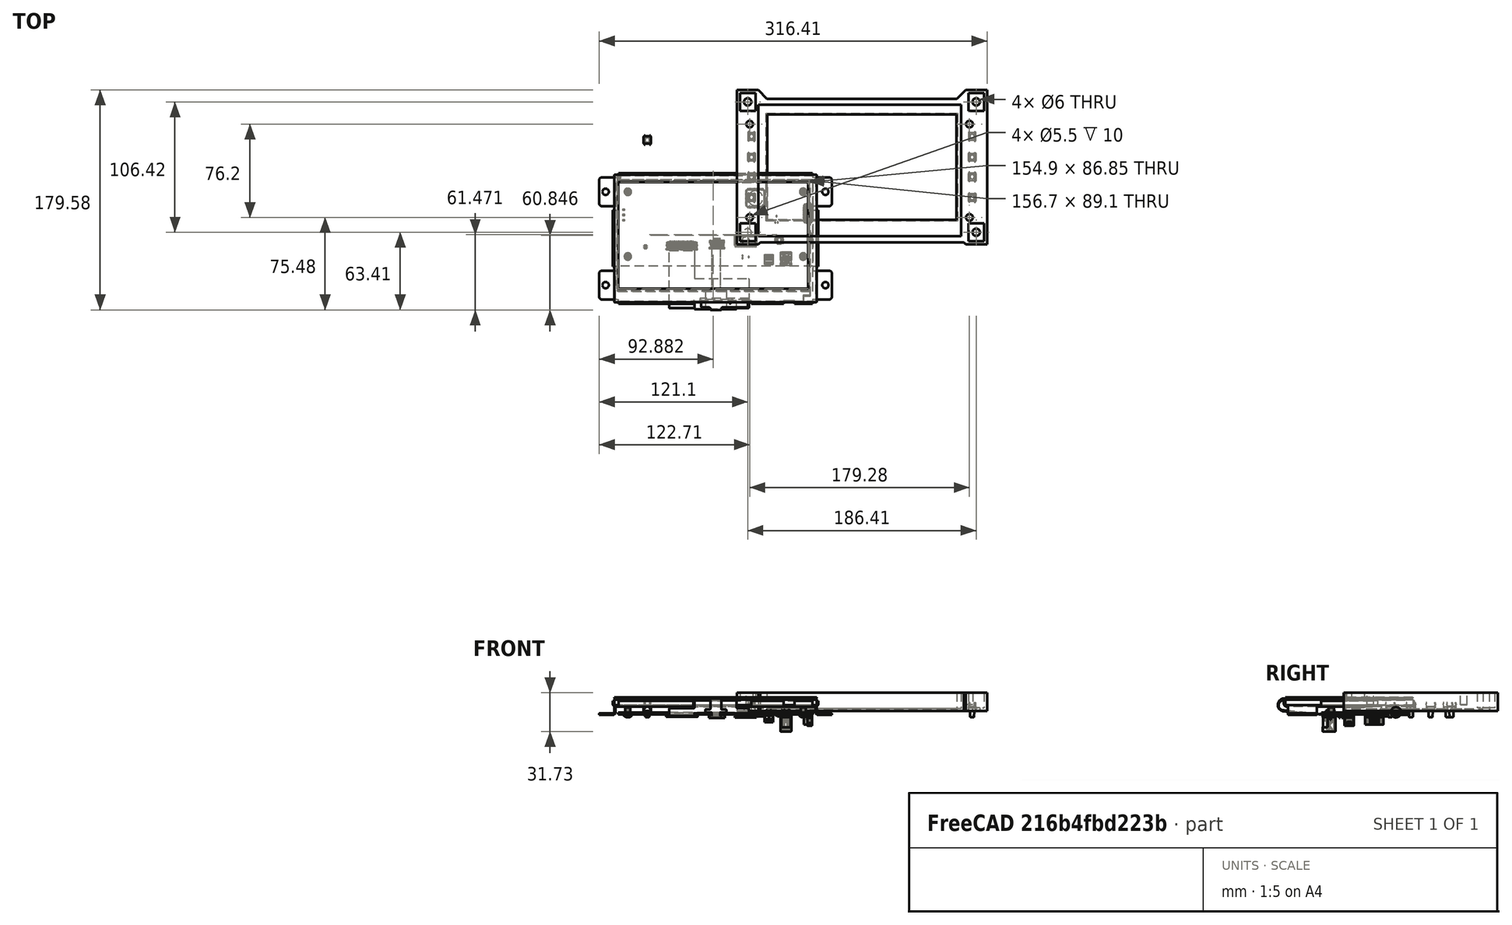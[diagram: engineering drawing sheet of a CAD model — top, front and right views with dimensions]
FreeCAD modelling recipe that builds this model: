
FCSTD DOCUMENT  (FreeCAD 0.18R4 (GitTag))
Label: front
License: All rights reserved
LicenseURL: http://en.wikipedia.org/wiki/All_rights_reserved
objects: Part::Feature×17, Sketcher::SketchObject×9, PartDesign::Pocket×6, PartDesign::Pad×1, PartDesign::Chamfer×1, PartDesign::Hole×1, App::Part×1, Mesh::Feature×1, PartDesign::Body×1
note: 44 computed .brp shape members not serialized (recipe doc carries the construction recipe); baked Part::Feature solids carry a one-line shape summary decoded from their .brp

FEATURE [Sketcher::SketchObject] Sketch  label="outerframe"
  MapMode = 5
  Support = -> [XY_Plane]
  sketch-geometry (4):
    g0: LineSegment StartX=0 StartY=0 StartZ=0 EndX=0 EndY=135.92 EndZ=0
    g1: LineSegment StartX=0 StartY=135.92 StartZ=0 EndX=204.21 EndY=135.92 EndZ=0
    g2: LineSegment StartX=204.21 StartY=135.92 StartZ=0 EndX=204.21 EndY=0 EndZ=0
    g3: LineSegment StartX=204.21 StartY=0 StartZ=0 EndX=0 EndY=0 EndZ=0
  constraints (11):
    c: Coincident(g0,g1)
    c: Coincident(g1,g2)
    c: Coincident(g2,g3)
    c: Coincident(g3,g0)
    c: Parallel(g3,g-1)
    c: Parallel(g0,g-2)
    c: Parallel(g2,g0)
    c: Parallel(g3,g1)
    c: DistanceY(g2,g1) = 135.92
    c: DistanceX(g0,g1) = 204.21
    c: Coincident(g0,g-1)
FEATURE [PartDesign::Pad] Pad  label="outer_frame"
  Length = 14.96
  Length2 = 100
  Profile = -> Sketch
  Type = 0
FEATURE [Sketcher::SketchObject] Sketch001  label="displayinlay"
  MapMode = 5
  Placement = pos=(0,0,14.96) rot=(0,0,1;0rad)
  Support = -> [Pad]
  sketch-geometry (4):
    g0: LineSegment StartX=17.65 StartY=118.77 StartZ=0 EndX=17.65 EndY=11.57 EndZ=0
    g1: LineSegment StartX=17.65 StartY=11.57 StartZ=0 EndX=182.95 EndY=11.57 EndZ=0
    g2: LineSegment StartX=182.95 StartY=11.57 StartZ=0 EndX=182.95 EndY=118.77 EndZ=0
    g3: LineSegment StartX=182.95 StartY=118.77 StartZ=0 EndX=17.65 EndY=118.77 EndZ=0
  constraints (12):
    c: Vertical(g0)
    c: Coincident(g0,g1)
    c: Horizontal(g1)
    c: Coincident(g1,g2)
    c: Coincident(g2,g3)
    c: Coincident(g3,g0)
    c: Horizontal(g3)
    c: Parallel(g0,g2)
    c: DistanceX(g0,g2) = 165.3
    c: DistanceY(g0,g0) = 107.2
    c: DistanceX(g-1,g0) = 17.65
    c: DistanceY(g-1,g0) = 11.57
FEATURE [PartDesign::Pocket] Pocket  label="display_inlay"
  BaseFeature = -> Pad
  Length = 12.96
  Length2 = 100
  Profile = -> Sketch001
  Type = 0
FEATURE [Sketcher::SketchObject] Sketch002  label="viewingarea"
  MapMode = 5
  Placement = pos=(0,0,14.96) rot=(0,0,1;0rad)
  Support = -> [Pocket]
  sketch-geometry (4):
    g0: LineSegment StartX=25 StartY=110.92 StartZ=0 EndX=25 EndY=25 EndZ=0
    g1: LineSegment StartX=25 StartY=25 StartZ=0 EndX=179.21 EndY=25 EndZ=0
    g2: LineSegment StartX=179.21 StartY=25 StartZ=0 EndX=179.21 EndY=110.92 EndZ=0
    g3: LineSegment StartX=179.21 StartY=110.92 StartZ=0 EndX=25 EndY=110.92 EndZ=0
  constraints (12):
    c: Vertical(g0)
    c: Coincident(g0,g1)
    c: Horizontal(g1)
    c: Coincident(g1,g2)
    c: Vertical(g2)
    c: Coincident(g2,g3)
    c: Coincident(g3,g0)
    c: Horizontal(g3)
    c: DistanceX(g0,g2) = 154.21
    c: DistanceY(g1,g2) = 85.92
    c: DistanceX(g-1,g0) = 25
    c: DistanceY(g-1,g0) = 25
FEATURE [PartDesign::Pocket] Pocket001  label="viewing_area"
  BaseFeature = -> Pocket
  Length = 14.96
  Length2 = 100
  Profile = -> Sketch002
  Type = 1
FEATURE [Sketcher::SketchObject] Sketch003  label="DisplayOutlines"
  MapMode = 5
  Placement = pos=(0,0,14.96) rot=(0,0,1;0rad)
  Support = -> [Pocket001]
  sketch-geometry (28):
    g0: LineSegment StartX=17.65 StartY=118.27 StartZ=0 EndX=17.65 EndY=11.57 EndZ=0
    g1: LineSegment StartX=17.65 StartY=11.57 StartZ=0 EndX=182.65 EndY=11.57 EndZ=0
    g2: LineSegment StartX=182.65 StartY=11.57 StartZ=0 EndX=182.65 EndY=118.27 EndZ=0
    g3: LineSegment StartX=182.65 StartY=118.27 StartZ=0 EndX=17.65 EndY=118.27 EndZ=0
    g4: LineSegment StartX=17.65 StartY=114.72 StartZ=0 EndX=17.65 EndY=91.32 EndZ=0
    g5: LineSegment StartX=17.65 StartY=91.32 StartZ=0 EndX=5.31 EndY=91.32 EndZ=0
    g6: LineSegment StartX=5.31 StartY=91.32 StartZ=0 EndX=5.31 EndY=114.72 EndZ=0
    g7: LineSegment StartX=5.31 StartY=114.72 StartZ=0 EndX=17.65 EndY=114.72 EndZ=0
    g8: Circle CenterX=10.51 CenterY=103.02 CenterZ=0 NormalX=0 NormalY=0 NormalZ=1 AngleXU=0 Radius=2.58
    g9: LineSegment StartX=5.31 StartY=38.52 StartZ=0 EndX=17.65 EndY=38.52 EndZ=0
    g10: LineSegment StartX=17.65 StartY=38.52 StartZ=0 EndX=17.65 EndY=15.12 EndZ=0
    g11: LineSegment StartX=17.65 StartY=15.12 StartZ=0 EndX=5.31 EndY=15.12 EndZ=0
    g12: LineSegment StartX=5.31 StartY=15.12 StartZ=0 EndX=5.31 EndY=38.52 EndZ=0
    g13: Circle CenterX=10.51 CenterY=26.82 CenterZ=0 NormalX=0 NormalY=0 NormalZ=1 AngleXU=0 Radius=2.58
    g14: LineSegment StartX=182.65 StartY=114.72 StartZ=0 EndX=194.99 EndY=114.72 EndZ=0
    g15: LineSegment StartX=194.99 StartY=114.72 StartZ=0 EndX=194.99 EndY=91.32 EndZ=0
    g16: LineSegment StartX=194.99 StartY=91.32 StartZ=0 EndX=182.65 EndY=91.32 EndZ=0
    g17: LineSegment StartX=182.65 StartY=91.32 StartZ=0 EndX=182.65 EndY=114.72 EndZ=0
    g18: Circle CenterX=189.79 CenterY=103.02 CenterZ=0 NormalX=0 NormalY=0 NormalZ=1 AngleXU=0 Radius=2.58
    g19: LineSegment StartX=182.65 StartY=38.52 StartZ=0 EndX=194.99 EndY=38.52 EndZ=0
    g20: LineSegment StartX=194.99 StartY=38.52 StartZ=0 EndX=194.99 EndY=15.12 EndZ=0
    g21: LineSegment StartX=194.99 StartY=15.12 StartZ=0 EndX=182.65 EndY=15.12 EndZ=0
    g22: LineSegment StartX=182.65 StartY=15.12 StartZ=0 EndX=182.65 EndY=38.52 EndZ=0
    g23: Circle CenterX=189.79 CenterY=26.82 CenterZ=0 NormalX=0 NormalY=0 NormalZ=1 AngleXU=0 Radius=2.58
    g24: LineSegment StartX=25 StartY=110.92 StartZ=0 EndX=25 EndY=25 EndZ=0
    g25: LineSegment StartX=25 StartY=25 StartZ=0 EndX=179.21 EndY=25 EndZ=0
    g26: LineSegment StartX=179.21 StartY=25 StartZ=0 EndX=179.21 EndY=110.92 EndZ=0
    g27: LineSegment StartX=179.21 StartY=110.92 StartZ=0 EndX=25 EndY=110.92 EndZ=0
  constraints (84):
    c: Vertical(g0)
    c: Coincident(g0,g1)
    c: Horizontal(g1)
    c: Coincident(g1,g2)
    c: Vertical(g2)
    c: Coincident(g2,g3)
    c: Parallel(g3,g1)
    c: Coincident(g3,g0)
    c: DistanceX(g0,g2) = 165
    c: DistanceY(g0,g0) = 106.7
    c: PointOnObject(g4,g0)
    c: Vertical(g4)
    c: Coincident(g4,g5)
    c: Horizontal(g5)
    c: Coincident(g5,g6)
    c: Coincident(g6,g7)
    c: Coincident(g7,g4)
    c: Parallel(g6,g0)
    c: Parallel(g7,g5)
    c: DistanceY(g5,g6) = 23.4
    c: DistanceX(g6,g4) = 12.34
    c: DistanceY(g4,g0) = 3.55
    c: Diameter(g8) = 5.16
    c: DistanceY(g8,g6) = 11.7
    c: DistanceX(g5,g8) = 5.2
    c: PointOnObject(g9,g0)
    c: Coincident(g9,g10)
    c: PointOnObject(g10,g0)
    c: Coincident(g10,g11)
    c: Coincident(g11,g12)
    c: Coincident(g12,g9)
    c: Parallel(g9,g11)
    c: Parallel(g12,g0)
    c: Perpendicular(g0,g9)
    c: DistanceY(g11,g9) = 23.4
    c: DistanceX(g9,g9) = 12.34
    c: DistanceY(g9,g5) = 52.8
    c: Diameter(g13) = 5.16
    c: DistanceY(g13,g9) = 11.7
    c: DistanceX(g9,g13) = 5.2
    c: PointOnObject(g14,g2)
    c: Horizontal(g14)
    c: Coincident(g14,g15)
    c: Vertical(g15)
    c: Coincident(g15,g16)
    c: Horizontal(g16)
    c: Coincident(g16,g17)
    c: Coincident(g17,g14)
    c: Vertical(g17)
    c: Diameter(g18) = 5.16
    c: DistanceX(g18,g14) = 5.2
    c: DistanceY(g18,g14) = 11.7
    c: DistanceY(g14,g2) = 3.55
    c: DistanceY(g15,g14) = 23.4
    c: DistanceX(g16,g15) = 12.34
    c: PointOnObject(g19,g2)
    c: Horizontal(g19)
    c: Coincident(g19,g20)
    c: Vertical(g20)
    c: Coincident(g20,g21)
    c: PointOnObject(g21,g2)
    c: Horizontal(g21)
    c: Coincident(g21,g22)
    c: Coincident(g22,g19)
    c: Diameter(g23) = 5.16
    c: DistanceX(g23,g19) = 5.2
    c: DistanceY(g19,g15) = 52.8
    c: DistanceY(g20,g19) = 23.4
    c: DistanceY(g20,g23) = 11.7
    c: DistanceX(g19,g19) = 12.34
    c: Vertical(g24)
    c: Coincident(g24,g25)
    c: Horizontal(g25)
    c: Coincident(g25,g26)
    c: Vertical(g26)
    c: Coincident(g26,g27)
    c: Coincident(g27,g24)
    c: Horizontal(g27)
    c: DistanceX(g24,g26) = 154.21
    c: DistanceY(g24,g24) = 85.92
    c: DistanceX(g10,g24) = 7.35
    c: DistanceY(g24,g0) = 7.35
    c: DistanceX(g-1,g24) = 25
    c: DistanceY(g-1,g24) = 25
FEATURE [Sketcher::SketchObject] Sketch005  label="EncoderCutOut"
  MapMode = 5
  Placement = pos=(0,0,14.96) rot=(0,0,1;0rad)
  sketch-geometry (16):
    g0: LineSegment StartX=2.5 StartY=128.42 StartZ=0 EndX=15.3 EndY=128.42 EndZ=0
    g1: LineSegment StartX=15.3 StartY=128.42 StartZ=0 EndX=15.3 EndY=113.92 EndZ=0
    g2: LineSegment StartX=15.3 StartY=113.92 StartZ=0 EndX=2.5 EndY=113.92 EndZ=0
    g3: LineSegment StartX=2.5 StartY=113.92 StartZ=0 EndX=2.5 EndY=128.42 EndZ=0
    g4: LineSegment StartX=188.91 StartY=128.42 StartZ=0 EndX=201.71 EndY=128.42 EndZ=0
    g5: LineSegment StartX=201.71 StartY=128.42 StartZ=0 EndX=201.71 EndY=113.92 EndZ=0
    g6: LineSegment StartX=201.71 StartY=113.92 StartZ=0 EndX=188.91 EndY=113.92 EndZ=0
    g7: LineSegment StartX=188.91 StartY=113.92 StartZ=0 EndX=188.91 EndY=128.42 EndZ=0
    g8: LineSegment StartX=2.5 StartY=22 StartZ=0 EndX=15.3 EndY=22 EndZ=0
    g9: LineSegment StartX=15.3 StartY=22 StartZ=0 EndX=15.3 EndY=7.5 EndZ=0
    g10: LineSegment StartX=15.3 StartY=7.5 StartZ=0 EndX=2.5 EndY=7.5 EndZ=0
    g11: LineSegment StartX=2.5 StartY=7.5 StartZ=0 EndX=2.5 EndY=22 EndZ=0
    g12: LineSegment StartX=188.91 StartY=22 StartZ=0 EndX=201.71 EndY=22 EndZ=0
    g13: LineSegment StartX=201.71 StartY=22 StartZ=0 EndX=201.71 EndY=7.5 EndZ=0
    g14: LineSegment StartX=201.71 StartY=7.5 StartZ=0 EndX=188.91 EndY=7.5 EndZ=0
    g15: LineSegment StartX=188.91 StartY=7.5 StartZ=0 EndX=188.91 EndY=22 EndZ=0
  constraints (48):
    c: Horizontal(g0)
    c: Coincident(g0,g1)
    c: Vertical(g1)
    c: Coincident(g1,g2)
    c: Horizontal(g2)
    c: Coincident(g2,g3)
    c: Coincident(g3,g0)
    c: Parallel(g3,g1)
    c: DistanceX(g0,g0) = 12.8
    c: DistanceY(g1,g0) = 14.5
    c: Horizontal(g4)
    c: Coincident(g4,g5)
    c: Vertical(g5)
    c: Coincident(g5,g6)
    c: Horizontal(g6)
    c: Coincident(g6,g7)
    c: Coincident(g7,g4)
    c: Parallel(g7,g5)
    c: Equal(g0,g4) = 12.8
    c: DistanceY(g5,g4) = 14.5
    c: Horizontal(g8)
    c: Coincident(g8,g9)
    c: Vertical(g9)
    c: Coincident(g9,g10)
    c: Horizontal(g10)
    c: Coincident(g10,g11)
    c: Coincident(g11,g8)
    c: Parallel(g11,g9)
    c: Equal(g0,g8) = 12.8
    c: DistanceY(g9,g8) = 14.5
    c: DistanceX(g-1,g10) = 2.5
    c: DistanceX(g-1,g2) = 2.5
    c: DistanceY(g-1,g10) = 7.5
    c: DistanceY(g-1,g0) = 128.42
    c: DistanceY(g-1,g4) = 128.42
    c: DistanceX(g-1,g4) = 201.71
    c: Horizontal(g12)
    c: Coincident(g12,g13)
    c: Vertical(g13)
    c: Coincident(g13,g14)
    c: Horizontal(g14)
    c: Coincident(g14,g15)
    c: Coincident(g15,g12)
    c: Parallel(g15,g13)
    c: DistanceY(g13,g12) = 14.5
    c: DistanceX(g12,g12) = 12.8
    c: DistanceY(g-1,g14) = 7.5
    c: DistanceX(g-1,g13) = 201.71
FEATURE [Sketcher::SketchObject] Sketch006  label="DisplayOutLinesHolesCut"
  MapMode = 5
  Placement = pos=(0,0,14.96) rot=(0,0,1;0rad)
  Support = -> [Pocket001]
  sketch-geometry (28):
    g0: LineSegment [constr] StartX=17.65 StartY=118.27 StartZ=0 EndX=17.65 EndY=11.57 EndZ=0
    g1: LineSegment [constr] StartX=17.65 StartY=11.57 StartZ=0 EndX=182.65 EndY=11.57 EndZ=0
    g2: LineSegment [constr] StartX=182.65 StartY=11.57 StartZ=0 EndX=182.65 EndY=118.27 EndZ=0
    g3: LineSegment [constr] StartX=182.65 StartY=118.27 StartZ=0 EndX=17.65 EndY=118.27 EndZ=0
    g4: LineSegment [constr] StartX=17.65 StartY=114.72 StartZ=0 EndX=17.65 EndY=91.32 EndZ=0
    g5: LineSegment [constr] StartX=17.65 StartY=91.32 StartZ=0 EndX=5.31 EndY=91.32 EndZ=0
    g6: LineSegment [constr] StartX=5.31 StartY=91.32 StartZ=0 EndX=5.31 EndY=114.72 EndZ=0
    g7: LineSegment [constr] StartX=5.31 StartY=114.72 StartZ=0 EndX=17.65 EndY=114.72 EndZ=0
    g8: Circle CenterX=10.51 CenterY=103.02 CenterZ=0 NormalX=0 NormalY=0 NormalZ=1 AngleXU=0 Radius=2.75
    g9: LineSegment [constr] StartX=5.31 StartY=38.52 StartZ=0 EndX=17.65 EndY=38.52 EndZ=0
    g10: LineSegment [constr] StartX=17.65 StartY=38.52 StartZ=0 EndX=17.65 EndY=15.12 EndZ=0
    g11: LineSegment [constr] StartX=17.65 StartY=15.12 StartZ=0 EndX=5.31 EndY=15.12 EndZ=0
    g12: LineSegment [constr] StartX=5.31 StartY=15.12 StartZ=0 EndX=5.31 EndY=38.52 EndZ=0
    g13: Circle CenterX=10.51 CenterY=26.82 CenterZ=0 NormalX=0 NormalY=0 NormalZ=1 AngleXU=0 Radius=2.75
    g14: LineSegment [constr] StartX=182.65 StartY=114.72 StartZ=0 EndX=194.99 EndY=114.72 EndZ=0
    g15: LineSegment [constr] StartX=194.99 StartY=114.72 StartZ=0 EndX=194.99 EndY=91.32 EndZ=0
    g16: LineSegment [constr] StartX=194.99 StartY=91.32 StartZ=0 EndX=182.65 EndY=91.32 EndZ=0
    g17: LineSegment [constr] StartX=182.65 StartY=91.32 StartZ=0 EndX=182.65 EndY=114.72 EndZ=0
    g18: Circle CenterX=189.79 CenterY=103.02 CenterZ=0 NormalX=0 NormalY=0 NormalZ=1 AngleXU=0 Radius=2.75
    g19: LineSegment [constr] StartX=182.65 StartY=38.52 StartZ=0 EndX=194.99 EndY=38.52 EndZ=0
    g20: LineSegment [constr] StartX=194.99 StartY=38.52 StartZ=0 EndX=194.99 EndY=15.12 EndZ=0
    g21: LineSegment [constr] StartX=194.99 StartY=15.12 StartZ=0 EndX=182.65 EndY=15.12 EndZ=0
    g22: LineSegment [constr] StartX=182.65 StartY=15.12 StartZ=0 EndX=182.65 EndY=38.52 EndZ=0
    g23: Circle CenterX=189.79 CenterY=26.82 CenterZ=0 NormalX=0 NormalY=0 NormalZ=1 AngleXU=0 Radius=2.75
    g24: LineSegment [constr] StartX=25 StartY=110.92 StartZ=0 EndX=25 EndY=25 EndZ=0
    g25: LineSegment [constr] StartX=25 StartY=25 StartZ=0 EndX=179.21 EndY=25 EndZ=0
    g26: LineSegment [constr] StartX=179.21 StartY=25 StartZ=0 EndX=179.21 EndY=110.92 EndZ=0
    g27: LineSegment [constr] StartX=179.21 StartY=110.92 StartZ=0 EndX=25 EndY=110.92 EndZ=0
  constraints (84):
    c: Vertical(g0)
    c: Coincident(g0,g1)
    c: Horizontal(g1)
    c: Coincident(g1,g2)
    c: Vertical(g2)
    c: Coincident(g2,g3)
    c: Parallel(g3,g1)
    c: Coincident(g3,g0)
    c: DistanceX(g0,g2) = 165
    c: DistanceY(g0,g0) = 106.7
    c: PointOnObject(g4,g0)
    c: Vertical(g4)
    c: Coincident(g4,g5)
    c: Horizontal(g5)
    c: Coincident(g5,g6)
    c: Coincident(g6,g7)
    c: Coincident(g7,g4)
    c: Parallel(g6,g0)
    c: Parallel(g7,g5)
    c: DistanceY(g5,g6) = 23.4
    c: DistanceX(g6,g4) = 12.34
    c: DistanceY(g4,g0) = 3.55
    c: Diameter(g8) = 5.5
    c: DistanceY(g8,g6) = 11.7
    c: DistanceX(g5,g8) = 5.2
    c: PointOnObject(g9,g0)
    c: Coincident(g9,g10)
    c: PointOnObject(g10,g0)
    c: Coincident(g10,g11)
    c: Coincident(g11,g12)
    c: Coincident(g12,g9)
    c: Parallel(g9,g11)
    c: Parallel(g12,g0)
    c: Perpendicular(g0,g9)
    c: DistanceY(g11,g9) = 23.4
    c: DistanceX(g9,g9) = 12.34
    c: DistanceY(g9,g5) = 52.8
    c: Diameter(g13) = 5.5
    c: DistanceY(g13,g9) = 11.7
    c: DistanceX(g9,g13) = 5.2
    c: PointOnObject(g14,g2)
    c: Horizontal(g14)
    c: Coincident(g14,g15)
    c: Vertical(g15)
    c: Coincident(g15,g16)
    c: Horizontal(g16)
    c: Coincident(g16,g17)
    c: Coincident(g17,g14)
    c: Vertical(g17)
    c: Diameter(g18) = 5.5
    c: DistanceX(g18,g14) = 5.2
    c: DistanceY(g18,g14) = 11.7
    c: DistanceY(g14,g2) = 3.55
    c: DistanceY(g15,g14) = 23.4
    c: DistanceX(g16,g15) = 12.34
    c: PointOnObject(g19,g2)
    c: Horizontal(g19)
    c: Coincident(g19,g20)
    c: Vertical(g20)
    c: Coincident(g20,g21)
    c: PointOnObject(g21,g2)
    c: Horizontal(g21)
    c: Coincident(g21,g22)
    c: Coincident(g22,g19)
    c: Diameter(g23) = 5.5
    c: DistanceX(g23,g19) = 5.2
    c: DistanceY(g19,g15) = 52.8
    c: DistanceY(g20,g19) = 23.4
    c: DistanceY(g20,g23) = 11.7
    c: DistanceX(g19,g19) = 12.34
    c: Vertical(g24)
    c: Coincident(g24,g25)
    c: Horizontal(g25)
    c: Coincident(g25,g26)
    c: Vertical(g26)
    c: Coincident(g26,g27)
    c: Coincident(g27,g24)
    c: Horizontal(g27)
    c: DistanceX(g24,g26) = 154.21
    c: DistanceY(g24,g24) = 85.92
    c: DistanceX(g10,g24) = 7.35
    c: DistanceY(g24,g0) = 7.35
    c: DistanceY(g-1,g24) = 25
    c: DistanceX(g-1,g24) = 25
FEATURE [PartDesign::Pocket] Pocket002  label="HolesDisplayMounting"
  BaseFeature = -> Pocket001
  Length = 10
  Length2 = 100
  Profile = -> Sketch006
  Type = 0
FEATURE [PartDesign::Chamfer] Chamfer
  Base = -> Pocket002 [Edge14,Edge13,Edge15,Edge12]
  BaseFeature = -> Pocket002
  Size = 1
FEATURE [Sketcher::SketchObject] Sketch007  label="EncoderCutOutHole"
  MapMode = 5
  Placement = pos=(0,0,14.96) rot=(0,0,1;0rad)
  sketch-geometry (32):
    g0: LineSegment [constr] StartX=2.5 StartY=128.42 StartZ=0 EndX=15.3 EndY=128.42 EndZ=0
    g1: LineSegment [constr] StartX=15.3 StartY=128.42 StartZ=0 EndX=15.3 EndY=113.92 EndZ=0
    g2: LineSegment [constr] StartX=15.3 StartY=113.92 StartZ=0 EndX=2.5 EndY=113.92 EndZ=0
    g3: LineSegment [constr] StartX=2.5 StartY=113.92 StartZ=0 EndX=2.5 EndY=128.42 EndZ=0
    g4: Circle CenterX=8.9 CenterY=121.17 CenterZ=0 NormalX=0 NormalY=0 NormalZ=1 AngleXU=0 Radius=3.5
    g5: LineSegment [constr] StartX=2.5 StartY=113.92 StartZ=0 EndX=15.3 EndY=128.42 EndZ=0
    g6: LineSegment [constr] StartX=15.3 StartY=113.92 StartZ=0 EndX=2.5 EndY=128.42 EndZ=0
    g7: GeomPoint X=8.9 Y=121.17 Z=0
    g8: LineSegment [constr] StartX=2.5 StartY=22 StartZ=0 EndX=15.3 EndY=22 EndZ=0
    g9: LineSegment [constr] StartX=15.3 StartY=22 StartZ=0 EndX=15.3 EndY=7.5 EndZ=0
    g10: LineSegment [constr] StartX=15.3 StartY=7.5 StartZ=0 EndX=2.5 EndY=7.5 EndZ=0
    g11: LineSegment [constr] StartX=2.5 StartY=7.5 StartZ=0 EndX=2.5 EndY=22 EndZ=0
    g12: Circle CenterX=8.9 CenterY=14.75 CenterZ=0 NormalX=0 NormalY=0 NormalZ=1 AngleXU=0 Radius=3.5
    g13: LineSegment [constr] StartX=2.5 StartY=7.5 StartZ=0 EndX=15.3 EndY=22 EndZ=0
    g14: LineSegment [constr] StartX=15.3 StartY=7.5 StartZ=0 EndX=2.5 EndY=22 EndZ=0
    g15: GeomPoint X=8.9 Y=14.75 Z=0
    g16: LineSegment [constr] StartX=188.91 StartY=128.42 StartZ=0 EndX=201.71 EndY=128.42 EndZ=0
    g17: LineSegment [constr] StartX=201.71 StartY=128.42 StartZ=0 EndX=201.71 EndY=113.92 EndZ=0
    g18: LineSegment [constr] StartX=201.71 StartY=113.92 StartZ=0 EndX=188.91 EndY=113.92 EndZ=0
    g19: LineSegment [constr] StartX=188.91 StartY=113.92 StartZ=0 EndX=188.91 EndY=128.42 EndZ=0
    g20: Circle CenterX=195.31 CenterY=121.17 CenterZ=0 NormalX=0 NormalY=0 NormalZ=1 AngleXU=0 Radius=3.5
    g21: LineSegment [constr] StartX=188.91 StartY=113.92 StartZ=0 EndX=201.71 EndY=128.42 EndZ=0
    g22: LineSegment [constr] StartX=201.71 StartY=113.92 StartZ=0 EndX=188.91 EndY=128.42 EndZ=0
    g23: GeomPoint X=195.31 Y=121.17 Z=0
    g24: LineSegment [constr] StartX=188.91 StartY=22 StartZ=0 EndX=201.71 EndY=22 EndZ=0
    g25: LineSegment [constr] StartX=201.71 StartY=22 StartZ=0 EndX=201.71 EndY=7.5 EndZ=0
    g26: LineSegment [constr] StartX=201.71 StartY=7.5 StartZ=0 EndX=188.91 EndY=7.5 EndZ=0
    g27: LineSegment [constr] StartX=188.91 StartY=7.5 StartZ=0 EndX=188.91 EndY=22 EndZ=0
    g28: Circle CenterX=195.31 CenterY=14.75 CenterZ=0 NormalX=0 NormalY=0 NormalZ=1 AngleXU=0 Radius=3.5
    g29: LineSegment [constr] StartX=188.91 StartY=7.5 StartZ=0 EndX=201.71 EndY=22 EndZ=0
    g30: LineSegment [constr] StartX=201.71 StartY=7.5 StartZ=0 EndX=188.91 EndY=22 EndZ=0
    g31: GeomPoint X=195.31 Y=14.75 Z=0
  constraints (84):
    c: Horizontal(g0)
    c: Coincident(g0,g1)
    c: Vertical(g1)
    c: Coincident(g1,g2)
    c: Horizontal(g2)
    c: Coincident(g2,g3)
    c: Coincident(g3,g0)
    c: Parallel(g3,g1)
    c: DistanceX(g0,g0) = 12.8
    c: DistanceY(g1,g0) = 14.5
    c: Diameter(g4) = 7
    c: Coincident(g5,g2)
    c: Coincident(g5,g0)
    c: Coincident(g6,g1)
    c: Coincident(g6,g0)
    c: PointOnObject(g7,g5)
    c: PointOnObject(g7,g6)
    c: DistanceY(g4,g7) = 0
    c: DistanceX(g7,g4) = 0
    c: Horizontal(g8)
    c: Coincident(g8,g9)
    c: Vertical(g9)
    c: Coincident(g9,g10)
    c: Horizontal(g10)
    c: Coincident(g10,g11)
    c: Coincident(g11,g8)
    c: Parallel(g11,g9)
    c: Equal(g0,g8) = 12.8
    c: DistanceY(g9,g8) = 14.5
    c: Equal(g4,g12) = 7
    c: Coincident(g13,g10)
    c: Coincident(g13,g8)
    c: Coincident(g14,g9)
    c: Coincident(g14,g8)
    c: PointOnObject(g15,g13)
    c: PointOnObject(g15,g14)
    c: DistanceY(g12,g15) = 0
    c: DistanceX(g15,g12) = 0
    c: Horizontal(g16)
    c: Coincident(g16,g17)
    c: Vertical(g17)
    c: Coincident(g17,g18)
    c: Horizontal(g18)
    c: Coincident(g18,g19)
    c: Coincident(g19,g16)
    c: Parallel(g19,g17)
    c: Equal(g0,g16) = 12.8
    c: DistanceY(g17,g16) = 14.5
    c: Equal(g4,g20) = 7
    c: Coincident(g21,g18)
    c: Coincident(g21,g16)
    c: Coincident(g22,g17)
    c: Coincident(g22,g16)
    c: PointOnObject(g23,g21)
    c: PointOnObject(g23,g22)
    c: DistanceY(g20,g23) = 0
    c: DistanceX(g23,g20) = 0
    c: Horizontal(g24)
    c: Coincident(g24,g25)
    c: Vertical(g25)
    c: Coincident(g25,g26)
    c: Horizontal(g26)
    c: Coincident(g26,g27)
    c: Coincident(g27,g24)
    c: Parallel(g27,g25)
    c: Equal(g0,g24) = 12.8
    c: DistanceY(g25,g24) = 14.5
    c: Equal(g4,g28) = 7
    c: Coincident(g29,g26)
    c: Coincident(g29,g24)
    c: Coincident(g30,g25)
    c: Coincident(g30,g24)
    c: PointOnObject(g31,g29)
    c: PointOnObject(g31,g30)
    c: DistanceY(g28,g31) = 0
    c: DistanceX(g31,g28) = 0
    c: DistanceX(g-1,g2) = 2.5
    c: DistanceX(g-1,g10) = 2.5
    c: DistanceX(g-1,g25) = 201.71
    c: DistanceX(g-1,g17) = 201.71
    c: DistanceY(g-1,g10) = 7.5
    c: DistanceY(g-1,g25) = 7.5
    c: DistanceY(g-1,g0) = 128.42
    c: DistanceY(g-1,g16) = 128.42
FEATURE [PartDesign::Pocket] Pocket003  label="EncoderPocket"
  BaseFeature = -> Chamfer
  Length = 12.46
  Length2 = 100
  Profile = -> Sketch005
  Type = 0
FEATURE [PartDesign::Hole] Hole  label="EncoderHoles"
  BaseFeature = -> Pocket003
  Depth = 25
  DepthType = 0
  Diameter = 6
  DrillPoint = 1
  DrillPointAngle = 118
  HoleCutCountersinkAngle = 90
  HoleCutDepth = 0
  HoleCutDiameter = 0
  HoleCutType = 0
  ModelActualThread = false
  Profile = -> Sketch007
  Tapered = false
  TaperedAngle = 90
  ThreadAngle = 0
  ThreadClass = 0
  ThreadCutOffInner = 0
  ThreadCutOffOuter = 0
  ThreadDirection = 0
  ThreadFit = 0
  ThreadPitch = 0
  ThreadSize = 0
  ThreadType = 0
  Threaded = false
FEATURE [Sketcher::SketchObject] Sketch008  label="Trim"
  MapMode = 5
  Placement = pos=(0,0,14.96) rot=(0,0,1;0rad)
  Support = -> [Hole]
  sketch-geometry (17):
    g0: LineSegment StartX=0 StartY=130.92 StartZ=0 EndX=0 EndY=135.92 EndZ=0
    g1: LineSegment StartX=0 StartY=135.92 StartZ=0 EndX=10 EndY=135.92 EndZ=0
    g2: LineSegment StartX=0 StartY=130.92 StartZ=0 EndX=17.5 EndY=130.92 EndZ=0
    g3: LineSegment StartX=17.5 StartY=130.92 StartZ=0 EndX=24.65 EndY=123.77 EndZ=0
    g4: LineSegment StartX=24.65 StartY=123.77 StartZ=0 EndX=179.56 EndY=123.77 EndZ=0
    g5: LineSegment StartX=179.56 StartY=123.77 StartZ=0 EndX=186.71 EndY=130.92 EndZ=0
    g6: LineSegment StartX=186.71 StartY=130.92 StartZ=0 EndX=204.21 EndY=130.92 EndZ=0
    g7: LineSegment StartX=204.21 StartY=130.92 StartZ=0 EndX=204.21 EndY=135.92 EndZ=0
    g8: LineSegment StartX=204.21 StartY=135.92 StartZ=0 EndX=0 EndY=135.92 EndZ=0
    g9: LineSegment StartX=0 StartY=0 StartZ=0 EndX=204.21 EndY=0 EndZ=0
    g10: LineSegment StartX=204.21 StartY=0 StartZ=0 EndX=204.21 EndY=5 EndZ=0
    g11: LineSegment StartX=204.21 StartY=5 StartZ=0 EndX=186.71 EndY=5 EndZ=0
    g12: LineSegment StartX=186.71 StartY=5 StartZ=0 EndX=185.14 EndY=6.57 EndZ=0
    g13: LineSegment StartX=185.14 StartY=6.57 StartZ=0 EndX=19.07 EndY=6.57 EndZ=0
    g14: LineSegment StartX=19.07 StartY=6.57 StartZ=0 EndX=17.5 EndY=5 EndZ=0
    g15: LineSegment StartX=17.5 StartY=5 StartZ=0 EndX=0 EndY=5 EndZ=0
    g16: LineSegment StartX=0 StartY=5 StartZ=0 EndX=0 EndY=0 EndZ=0
  constraints (50):
    c: DistanceX(g-1,g1) = 10
    c: DistanceY(g-1,g1) = 135.92
    c: Coincident(g0,g1)
    c: Horizontal(g1)
    c: Horizontal(g2)
    c: Coincident(g2,g3)
    c: Coincident(g3,g4)
    c: Horizontal(g4)
    c: Coincident(g4,g5)
    c: Coincident(g5,g6)
    c: Horizontal(g6)
    c: Coincident(g6,g7)
    c: Vertical(g7)
    c: Coincident(g7,g8)
    c: Coincident(g8,g0)
    c: Horizontal(g8)
    c: Coincident(g2,g0)
    c: Parallel(g7,g0)
    c: DistanceX(g-1,g0) = 0
    c: DistanceX(g-1,g7) = 204.21
    c: Angle(g5) = 0.785398
    c: Angle(g3) = -0.785398
    c: DistanceY(g6,g0) = 0
    c: DistanceX(g-1,g2) = 17.5
    c: DistanceX(g-1,g5) = 186.71
    c: DistanceY(g-1,g2) = 130.92
    c: DistanceY(g-1,g3) = 123.77
    c: Coincident(g-1,g9)
    c: PointOnObject(g9,g-1)
    c: Coincident(g9,g10)
    c: Coincident(g10,g11)
    c: Coincident(g11,g12)
    c: Coincident(g12,g13)
    c: Horizontal(g13)
    c: Coincident(g13,g14)
    c: Coincident(g14,g15)
    c: Coincident(g15,g16)
    c: Coincident(g16,g9)
    c: Vertical(g16)
    c: Parallel(g15,g9)
    c: Parallel(g11,g9)
    c: Angle(g12) = 2.35619
    c: Angle(g14) = -2.35619
    c: Perpendicular(g9,g10)
    c: DistanceX(g9,g9) = 204.21
    c: DistanceY(g9,g15) = 5
    c: DistanceY(g11,g14) = 0
    c: DistanceY(g9,g13) = 6.57
    c: DistanceX(g9,g14) = 17.5
    c: DistanceX(g9,g11) = 186.71
FEATURE [Part::Feature] Part__Feature007  label="SCREW_95836A206"
  Placement = pos=(-88.858,-5.03851,2.22572) rot=(-0.001042,0.999999,0;3.14159rad)
  shape: bbox 6.495 x 6.495 x 7.739 mm, 90 faces (baked)
FEATURE [Part::Feature] Part__Feature004  label="SCREW_95836A203"
  Placement = pos=(54.142,47.7615,2.22572) rot=(0.112264,0.993678,0;3.14159rad)
  shape: bbox 6.516 x 6.331 x 7.739 mm, 90 faces (baked)
FEATURE [Part::Feature] Part__Feature006  label="SCREW_95836A205"
  Placement = pos=(-88.858,47.7615,2.22572) rot=(-0.100524,0.994935,0;3.14159rad)
  shape: bbox 6.449 x 6.363 x 7.739 mm, 90 faces (baked)
FEATURE [Part::Feature] Part__Feature005  label="SCREW_95836A204"
  Placement = pos=(54.142,-5.03851,2.22572) rot=(-0.016203,0.999869,0;3.14159rad)
  shape: bbox 6.491 x 6.491 x 7.739 mm, 90 faces (baked)
FEATURE [Part::Feature] Part__Feature  label="NHD-7.0-Mount"
  Placement = pos=(-66.5026,-96.831,-149.328) rot=(0,0,1;0rad)
  shape: bbox 189.7 x 106.7 x 11.46 mm, 298 faces, 5 solids (baked)
FEATURE [Part::Feature] Part__Feature001  label="NHD-7.0-1024600AF-LSXP"
  Placement = pos=(-17.358,9.66149,4.82572) rot=(0,0,1;0rad)
  shape: bbox 165 x 109.7 x 14.12 mm, 201 faces (baked)
FEATURE [Part::Feature] Part__Feature003  label="NHD-7.0-HDMI_PCB"
  Placement = pos=(-100.679,-3.63887,23.5082) rot=(0,1,0;3.14159rad)
  shape: bbox 159 x 68.8 x 17.6 mm, 5848 faces, 33 solids (baked)
FEATURE [Part::Feature] Part__Feature002  label="NHD-CTP-7.0K-HR"
  Placement = pos=(-14.4254,7.67152,10.6757) rot=(0,0,1;0rad)
  shape: bbox 165 x 110.3 x 15.54 mm, 144 faces, 8 solids (baked)
FEATURE [App::Part] NHD_7_0_HDMI_HR_RSXP_CTU  label="NHD-7.0-HDMI-HR-RSXP-CTU"
  Group = -> [Part__Feature,Part__Feature001,Part__Feature002,Part__Feature003,Part__Feature004,Part__Feature005,Part__Feature006,Part__Feature007]
  Origin = -> Origin001
  Placement = pos=(83,55,13) rot=(0,1,0;3.14159rad)
FEATURE [Mesh::Feature] Raspberry_Pi_3_Light_Version
  Placement = pos=(39,118,19) rot=(0,0,-1;1.5708rad)
FEATURE [Part::Feature] Part__Feature008  label="C-3-1825910-5"
  Placement = pos=(-73,90,-5) rot=(1,0,0;3.14159rad)
  shape: bbox 5.99 x 7.8 x 12.01 mm, 99 faces (baked)
FEATURE [Sketcher::SketchObject] Sketch009  label="PushButtonCutOut"
  MapMode = 5
  Support = -> [XY_Plane]
  sketch-geometry (56):
    g0: LineSegment StartX=9.15 StartY=89.92 StartZ=0 EndX=15.15 EndY=89.92 EndZ=0
    g1: LineSegment StartX=15.15 StartY=89.92 StartZ=0 EndX=15.15 EndY=95.92 EndZ=0
    g2: LineSegment StartX=15.15 StartY=95.92 StartZ=0 EndX=9.15 EndY=95.92 EndZ=0
    g3: LineSegment StartX=9.15 StartY=95.92 StartZ=0 EndX=9.15 EndY=89.92 EndZ=0
    g4: LineSegment StartX=9.15 StartY=79.28 StartZ=0 EndX=15.15 EndY=79.28 EndZ=0
    g5: LineSegment StartX=15.15 StartY=79.28 StartZ=0 EndX=15.15 EndY=73.28 EndZ=0
    g6: LineSegment StartX=15.15 StartY=73.28 StartZ=0 EndX=9.15 EndY=73.28 EndZ=0
    g7: LineSegment StartX=9.15 StartY=73.28 StartZ=0 EndX=9.15 EndY=79.28 EndZ=0
    g8: LineSegment StartX=9.15 StartY=62.64 StartZ=0 EndX=15.15 EndY=62.64 EndZ=0
    g9: LineSegment StartX=15.15 StartY=62.64 StartZ=0 EndX=15.15 EndY=56.64 EndZ=0
    g10: LineSegment StartX=15.15 StartY=56.64 StartZ=0 EndX=9.15 EndY=56.64 EndZ=0
    g11: LineSegment StartX=9.15 StartY=56.64 StartZ=0 EndX=9.15 EndY=62.64 EndZ=0
    g12: LineSegment StartX=9.15 StartY=46 StartZ=0 EndX=15.15 EndY=46 EndZ=0
    g13: LineSegment StartX=15.15 StartY=46 StartZ=0 EndX=15.15 EndY=40 EndZ=0
    g14: LineSegment StartX=15.15 StartY=40 StartZ=0 EndX=9.15 EndY=40 EndZ=0
    g15: LineSegment StartX=9.15 StartY=40 StartZ=0 EndX=9.15 EndY=46 EndZ=0
    g16: LineSegment [constr] StartX=9.15 StartY=95.92 StartZ=0 EndX=15.15 EndY=89.92 EndZ=0
    g17: LineSegment [constr] StartX=15.15 StartY=95.92 StartZ=0 EndX=9.15 EndY=89.92 EndZ=0
    g18: GeomPoint X=12.15 Y=92.92 Z=0
    g19: LineSegment [constr] StartX=9.15 StartY=73.28 StartZ=0 EndX=15.15 EndY=79.28 EndZ=0
    g20: LineSegment [constr] StartX=15.15 StartY=73.28 StartZ=0 EndX=9.15 EndY=79.28 EndZ=0
    g21: GeomPoint X=12.15 Y=76.28 Z=0
    g22: LineSegment [constr] StartX=9.15 StartY=56.64 StartZ=0 EndX=15.15 EndY=62.64 EndZ=0
    g23: LineSegment [constr] StartX=15.15 StartY=56.64 StartZ=0 EndX=9.15 EndY=62.64 EndZ=0
    g24: GeomPoint X=12.15 Y=59.64 Z=0
    g25: LineSegment [constr] StartX=15.15 StartY=46 StartZ=0 EndX=9.15 EndY=40 EndZ=0
    g26: LineSegment [constr] StartX=9.15 StartY=46 StartZ=0 EndX=15.15 EndY=40 EndZ=0
    g27: GeomPoint X=12.15 Y=43 Z=0
    g28: LineSegment StartX=189.06 StartY=89.92 StartZ=0 EndX=195.06 EndY=89.92 EndZ=0
    g29: LineSegment StartX=195.06 StartY=89.92 StartZ=0 EndX=195.06 EndY=95.92 EndZ=0
    g30: LineSegment StartX=195.06 StartY=95.92 StartZ=0 EndX=189.06 EndY=95.92 EndZ=0
    g31: LineSegment StartX=189.06 StartY=95.92 StartZ=0 EndX=189.06 EndY=89.92 EndZ=0
    g32: LineSegment StartX=189.06 StartY=79.28 StartZ=0 EndX=195.06 EndY=79.28 EndZ=0
    g33: LineSegment StartX=195.06 StartY=79.28 StartZ=0 EndX=195.06 EndY=73.28 EndZ=0
    g34: LineSegment StartX=195.06 StartY=73.28 StartZ=0 EndX=189.06 EndY=73.28 EndZ=0
    g35: LineSegment StartX=189.06 StartY=73.28 StartZ=0 EndX=189.06 EndY=79.28 EndZ=0
    g36: LineSegment StartX=189.06 StartY=62.64 StartZ=0 EndX=195.06 EndY=62.64 EndZ=0
    g37: LineSegment StartX=195.06 StartY=62.64 StartZ=0 EndX=195.06 EndY=56.64 EndZ=0
    g38: LineSegment StartX=195.06 StartY=56.64 StartZ=0 EndX=189.06 EndY=56.64 EndZ=0
    g39: LineSegment StartX=189.06 StartY=56.64 StartZ=0 EndX=189.06 EndY=62.64 EndZ=0
    g40: LineSegment StartX=189.06 StartY=46 StartZ=0 EndX=195.06 EndY=46 EndZ=0
    g41: LineSegment StartX=195.06 StartY=46 StartZ=0 EndX=195.06 EndY=40 EndZ=0
    g42: LineSegment StartX=195.06 StartY=40 StartZ=0 EndX=189.06 EndY=40 EndZ=0
    g43: LineSegment StartX=189.06 StartY=40 StartZ=0 EndX=189.06 EndY=46 EndZ=0
    g44: LineSegment [constr] StartX=189.06 StartY=95.92 StartZ=0 EndX=195.06 EndY=89.92 EndZ=0
    g45: LineSegment [constr] StartX=195.06 StartY=95.92 StartZ=0 EndX=189.06 EndY=89.92 EndZ=0
    g46: GeomPoint X=192.06 Y=92.92 Z=0
    g47: LineSegment [constr] StartX=189.06 StartY=73.28 StartZ=0 EndX=195.06 EndY=79.28 EndZ=0
    g48: LineSegment [constr] StartX=195.06 StartY=73.28 StartZ=0 EndX=189.06 EndY=79.28 EndZ=0
    g49: GeomPoint X=192.06 Y=76.28 Z=0
    g50: LineSegment [constr] StartX=189.06 StartY=56.64 StartZ=0 EndX=195.06 EndY=62.64 EndZ=0
    g51: LineSegment [constr] StartX=195.06 StartY=56.64 StartZ=0 EndX=189.06 EndY=62.64 EndZ=0
    g52: GeomPoint X=192.06 Y=59.64 Z=0
    g53: LineSegment [constr] StartX=195.06 StartY=46 StartZ=0 EndX=189.06 EndY=40 EndZ=0
    g54: LineSegment [constr] StartX=189.06 StartY=46 StartZ=0 EndX=195.06 EndY=40 EndZ=0
    g55: GeomPoint X=192.06 Y=43 Z=0
  constraints (140):
    c: Coincident(g0,g1)
    c: Coincident(g1,g2)
    c: Coincident(g2,g3)
    c: Coincident(g3,g0)
    c: Horizontal(g0)
    c: Horizontal(g2)
    c: Vertical(g1)
    c: Vertical(g3)
    c: Equal(g0,g3)
    c: DistanceX(g0,g0) = 6
    c: Coincident(g4,g5)
    c: Coincident(g5,g6)
    c: Coincident(g6,g7)
    c: Coincident(g7,g4)
    c: Horizontal(g4)
    c: Horizontal(g6)
    c: Vertical(g5)
    c: Vertical(g7)
    c: Equal(g4,g7)
    c: Equal(g0,g4) = 6
    c: Coincident(g8,g9)
    c: Coincident(g9,g10)
    c: Coincident(g10,g11)
    c: Coincident(g11,g8)
    c: Horizontal(g8)
    c: Horizontal(g10)
    c: Vertical(g9)
    c: Vertical(g11)
    c: Equal(g8,g11)
    c: Equal(g0,g8) = 6
    c: Coincident(g12,g13)
    c: Coincident(g13,g14)
    c: Coincident(g14,g15)
    c: Coincident(g15,g12)
    c: Horizontal(g12)
    c: Horizontal(g14)
    c: Vertical(g13)
    c: Vertical(g15)
    c: Equal(g12,g15)
    c: Equal(g0,g12) = 6
    c: DistanceX(g4,g2) = 0
    c: DistanceX(g8,g6) = 0
    c: DistanceX(g12,g10) = 0
    c: Coincident(g16,g2)
    c: Coincident(g16,g0)
    c: Coincident(g17,g1)
    c: Coincident(g17,g0)
    c: PointOnObject(g18,g17)
    c: PointOnObject(g18,g16)
    c: Coincident(g19,g6)
    c: Coincident(g19,g4)
    c: Coincident(g20,g5)
    c: Coincident(g20,g4)
    c: PointOnObject(g21,g20)
    c: PointOnObject(g21,g19)
    c: Coincident(g22,g10)
    c: Coincident(g22,g8)
    c: Coincident(g23,g9)
    c: Coincident(g23,g8)
    c: PointOnObject(g24,g23)
    c: Symmetric(g18,g24,g21)
    c: Coincident(g25,g12)
    c: Coincident(g25,g14)
    c: Coincident(g26,g12)
    c: Coincident(g26,g13)
    c: PointOnObject(g27,g26)
    c: Symmetric(g21,g27,g24)
    c: DistanceY(g-1,g2) = 95.92
    c: DistanceY(g-1,g14) = 40
    c: Coincident(g28,g29)
    c: Coincident(g29,g30)
    c: Coincident(g30,g31)
    c: Coincident(g31,g28)
    c: Horizontal(g28)
    c: Horizontal(g30)
    c: Vertical(g29)
    c: Vertical(g31)
    c: Equal(g28,g31)
    c: Equal(g0,g28) = 6
    c: Coincident(g32,g33)
    c: Coincident(g33,g34)
    c: Coincident(g34,g35)
    c: Coincident(g35,g32)
    c: Horizontal(g32)
    c: Horizontal(g34)
    c: Vertical(g33)
    c: Vertical(g35)
    c: Equal(g32,g35)
    c: Equal(g28,g32) = 6
    c: Coincident(g36,g37)
    c: Coincident(g37,g38)
    c: Coincident(g38,g39)
    c: Coincident(g39,g36)
    c: Horizontal(g36)
    c: Horizontal(g38)
    c: Vertical(g37)
    c: Vertical(g39)
    c: Equal(g36,g39)
    c: Equal(g28,g36) = 6
    c: Coincident(g40,g41)
    c: Coincident(g41,g42)
    c: Coincident(g42,g43)
    c: Coincident(g43,g40)
    c: Horizontal(g40)
    c: Horizontal(g42)
    c: Vertical(g41)
    c: Vertical(g43)
    c: Equal(g40,g43)
    c: Equal(g28,g40) = 6
    c: DistanceX(g32,g30) = 0
    c: DistanceX(g36,g34) = 0
    c: DistanceX(g40,g38) = 0
    c: Coincident(g44,g30)
    c: Coincident(g44,g28)
    c: Coincident(g45,g29)
    c: Coincident(g45,g28)
    c: PointOnObject(g46,g45)
    c: PointOnObject(g46,g44)
    c: Coincident(g47,g34)
    c: Coincident(g47,g32)
    c: Coincident(g48,g33)
    c: Coincident(g48,g32)
    c: PointOnObject(g49,g48)
    c: PointOnObject(g49,g47)
    c: Coincident(g50,g38)
    c: Coincident(g50,g36)
    c: Coincident(g51,g37)
    c: Coincident(g51,g36)
    c: PointOnObject(g52,g51)
    c: Symmetric(g46,g52,g49)
    c: Coincident(g53,g40)
    c: Coincident(g53,g42)
    c: Coincident(g54,g40)
    c: Coincident(g54,g41)
    c: PointOnObject(g55,g54)
    c: Symmetric(g49,g55,g52)
    c: DistanceY(g1,g30) = 0
    c: DistanceY(g42,g13) = 0
    c: DistanceX(g-1,g0) = 15.15
    c: DistanceX(g-1,g32) = 189.06
FEATURE [PartDesign::Pocket] Pocket004  label="PushButtonCuts"
  BaseFeature = -> Hole
  Length = 3.8
  Length2 = 100
  Profile = -> Sketch009
  Reversed = true
  Type = 0
FEATURE [PartDesign::Pocket] Pocket005  label="FrameTrim"
  BaseFeature = -> Pocket004
  Length = 5
  Length2 = 100
  Profile = -> Sketch008
  Type = 1
FEATURE [PartDesign::Body] Body
  Group = -> [Sketch,Pad,Sketch001,Pocket,Sketch002,Pocket001,Sketch006,Pocket002,Chamfer,Sketch005,Pocket003,Sketch007,Hole,Sketch009,Pocket004,Sketch008,Pocket005]
  Origin = -> Origin
  Tip = -> Pocket005
FEATURE [Part::Feature] Part__Feature009  label="pushbutton-001"
  Placement = pos=(192,43,-5) rot=(1,0,0;3.14159rad)
  shape: bbox 5.99 x 7.8 x 12.01 mm, 99 faces (baked)
FEATURE [Part::Feature] Part__Feature010  label="pushbutton-002"
  Placement = pos=(192,60,-5) rot=(1,0,0;3.14159rad)
  shape: bbox 5.99 x 7.8 x 12.01 mm, 99 faces (baked)
FEATURE [Part::Feature] Part__Feature011  label="pushbutton-003"
  Placement = pos=(192,76,-5) rot=(1,0,0;3.14159rad)
  shape: bbox 5.99 x 7.8 x 12.01 mm, 99 faces (baked)
FEATURE [Part::Feature] Part__Feature012  label="pushbutton-004"
  Placement = pos=(192,93,-5) rot=(1,0,0;3.14159rad)
  shape: bbox 5.99 x 7.8 x 12.01 mm, 99 faces (baked)
FEATURE [Part::Feature] Part__Feature013  label="pushbutton-005"
  Placement = pos=(12,93,-5) rot=(1,0,0;3.14159rad)
  shape: bbox 5.99 x 7.8 x 12.01 mm, 99 faces (baked)
FEATURE [Part::Feature] Part__Feature014  label="pushbutton-006"
  Placement = pos=(12,76,-5) rot=(1,0,0;3.14159rad)
  shape: bbox 5.99 x 7.8 x 12.01 mm, 99 faces (baked)
FEATURE [Part::Feature] Part__Feature015  label="pushbutton-007"
  Placement = pos=(12,60,-5) rot=(1,0,0;3.14159rad)
  shape: bbox 5.99 x 7.8 x 12.01 mm, 99 faces (baked)
FEATURE [Part::Feature] Part__Feature016  label="pushbutton-008"
  Placement = pos=(12,43,-5) rot=(1,0,0;3.14159rad)
  shape: bbox 5.99 x 7.8 x 12.01 mm, 99 faces (baked)
